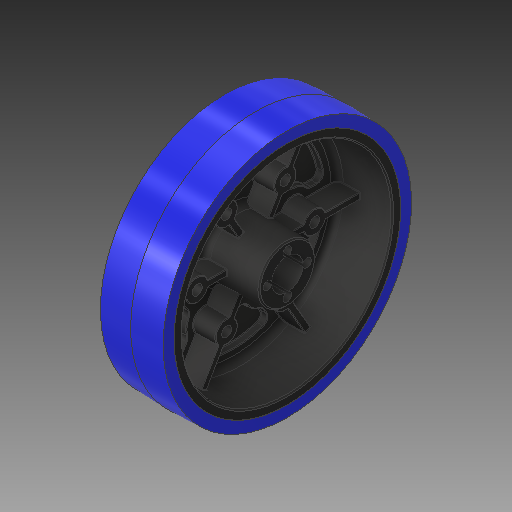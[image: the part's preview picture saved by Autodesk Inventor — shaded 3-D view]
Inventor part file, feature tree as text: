
AUTODESK INVENTOR PART (.ipt)
format: ipt  version: 2017 (Build 210142000, 142)  size: 1,480,192 bytes
history: native  units: in
note: dims shown in document units (in); Inventor stores cm internally (conversion verified against a paired STEP export)
features: other x2, extrude x1, sketch x1
ambient origin geometry x8: Origin, YZ Plane, XZ Plane, XY Plane, X Axis, Y Axis, Z Axis, Center Point
bodies: Solid1 (feature_tree), Solid2 (feature_tree)
feature tree (4):
  extrude  "Extrusion1"  Depth=1.0in TaperAngle=0.0deg
  sketch  "Sketch1"  dims[d0=0.5in d1=1.0in d2=0.0in]
  other  "4in Wheel Intergreated Hub 8mm Rev2_1:1"
  other  "4in Tread_2:1"
